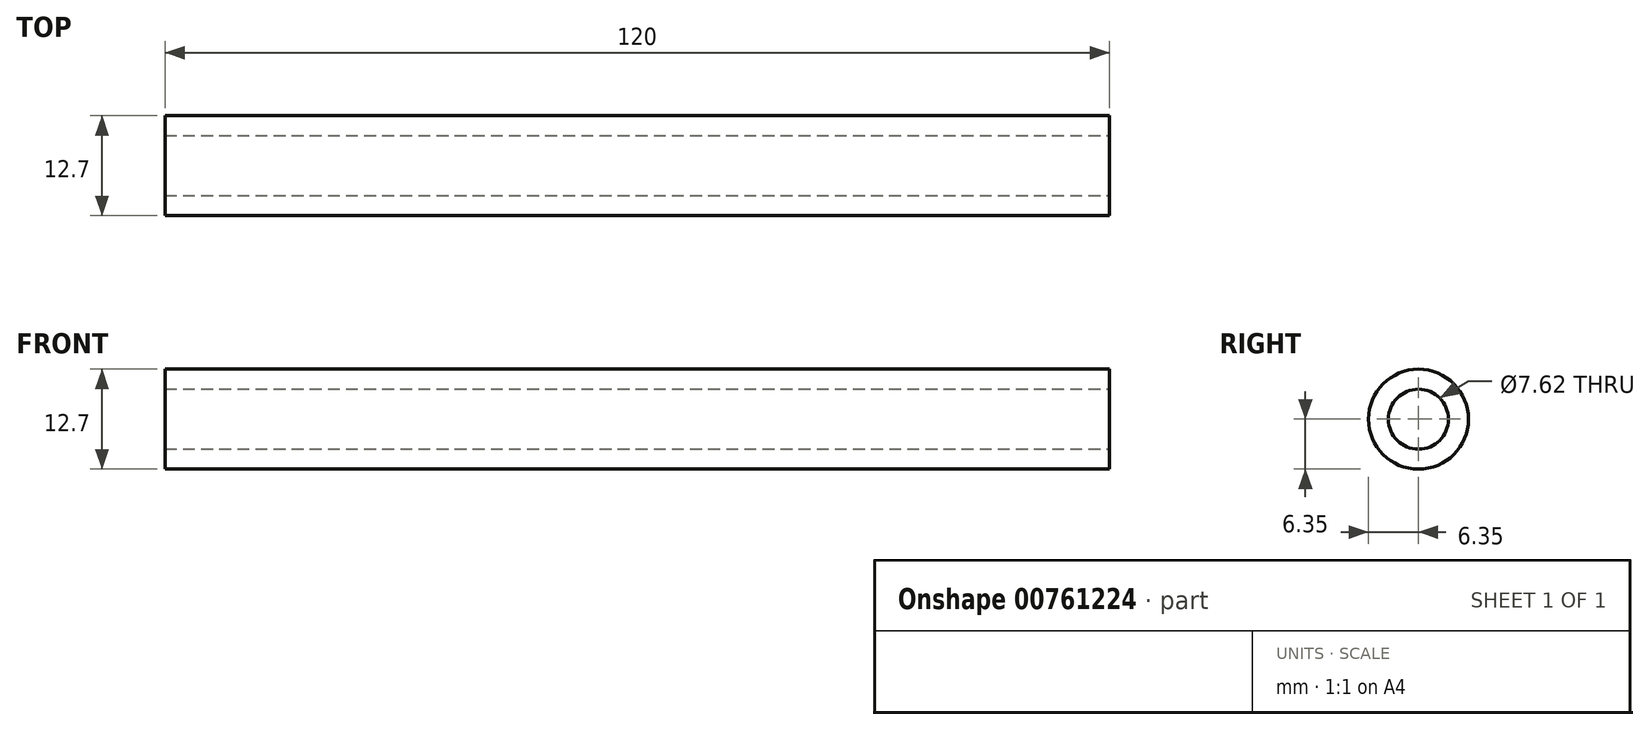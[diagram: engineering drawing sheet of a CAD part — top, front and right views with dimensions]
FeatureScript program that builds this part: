
annotation { "Feature Type Name" : "Feature", "Feature Type Description" : "" }
export const myFeature = defineFeature(function(context is Context, id is Id, definition is map)
    precondition{}
    {
        {
            var Q0;
            Q0=qCreatedBy(makeId("Front.planeOp"),FACE);
            var sketch = newSketch(context, id + "F0", { "sketchPlane" : qUnion([Q0])});
            skLineSegment(sketch, "E0", {"start": v(0, 3.8) * mm, "end": v(-120, 3.8) * mm});
            skLineSegment(sketch, "E1", {"start": v(-120, 3.8) * mm, "end": v(-120, 6.35) * mm});
            skLineSegment(sketch, "E2", {"start": v(-120, 6.35) * mm, "end": v(0, 6.35) * mm});
            skLineSegment(sketch, "E3", {"start": v(0, 6.35) * mm, "end": v(0, 3.8) * mm});
            skLineSegment(sketch, "E4", {"start": v(0, 0) * mm, "end": v(-120, 0) * mm, "construction": true});
            skSolve(sketch);
        }
        {
            var Q0;
            Q0=makeQuery(id+"F0.imprint","IMPRINT",FACE,{"disambiguationData":[TD([[makeQuery(id+"F0.imprint","IMPRINT",EDGE,{"derivedFrom":sQuery(id+"F0.wireOp",EDGE,"E0")}),-1.0]])]});
            var Q1;
            Q1=sQuery(id+"F0.wireOp",EDGE,"E1");
            var Q2;
            Q2=sQuery(id+"F0.wireOp",EDGE,"E2");
            var Q3;
            Q3=sQuery(id+"F0.wireOp",EDGE,"E3");
            var Q4;
            Q4=sQuery(id+"F0.wireOp",EDGE,"E0");
            var Q5;
            Q5=sQuery(id+"F0.wireOp",EDGE,"E4");
            revolve(context, id + "F1", {"surfaceOperationType" : NewSurfaceOperationType.NEW, "entities" : qUnion([Q0]), "surfaceEntities" : qUnion([Q1, Q2, Q3, Q4]), "axis" : qUnion([Q5]), "revolveType" : RevolveType.FULL});
        }
    });
